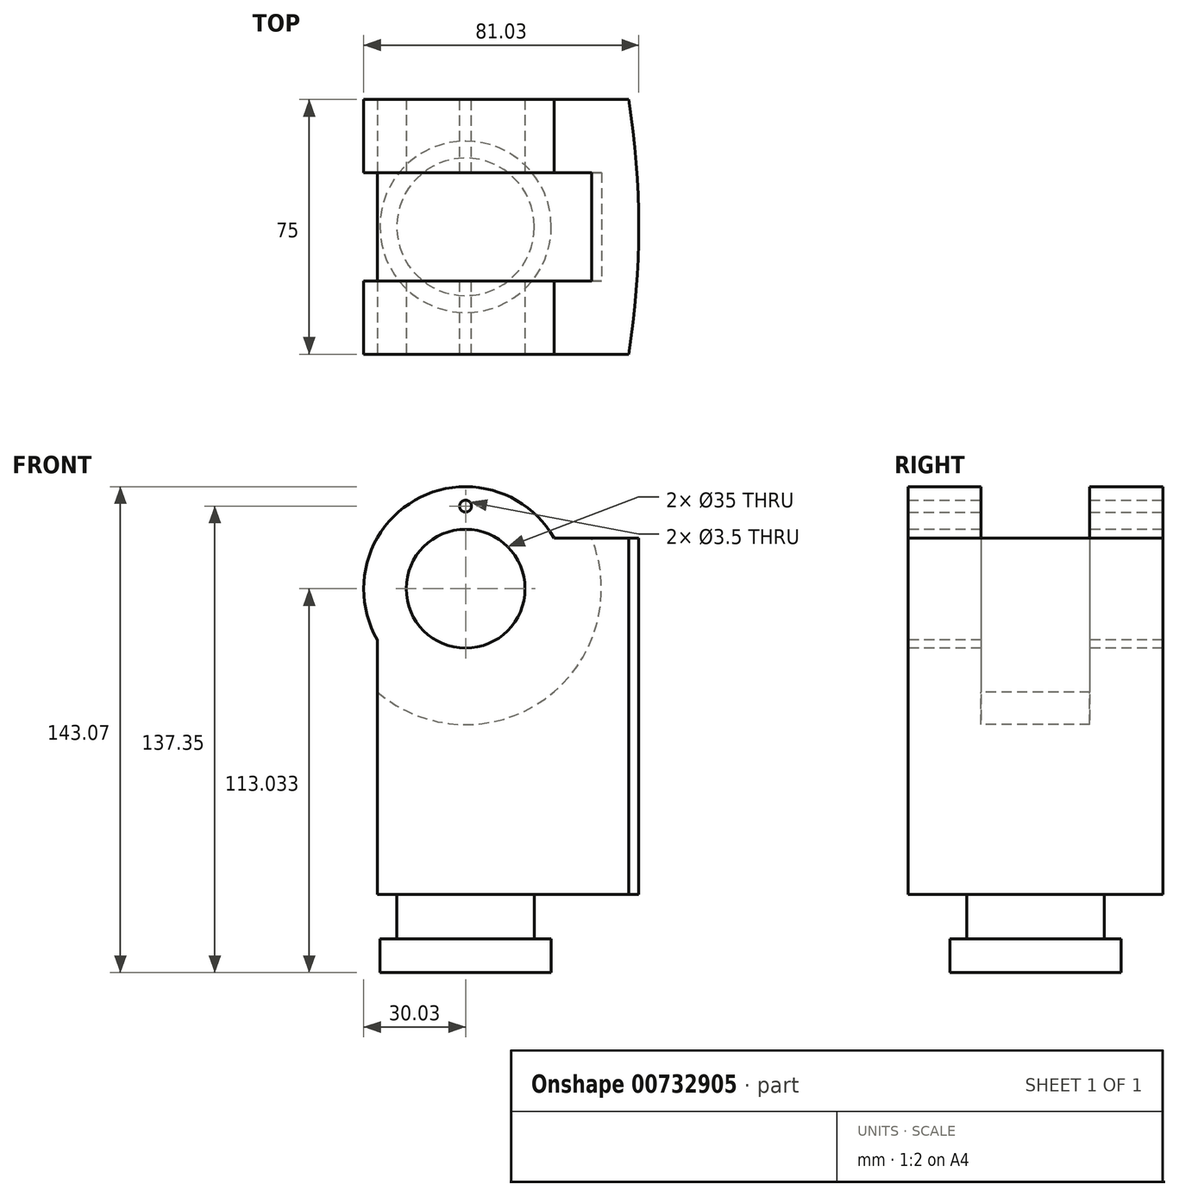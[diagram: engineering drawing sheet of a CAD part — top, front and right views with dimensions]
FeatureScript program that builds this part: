
annotation { "Feature Type Name" : "Feature", "Feature Type Description" : "" }
export const myFeature = defineFeature(function(context is Context, id is Id, definition is map)
    precondition{}
    {
        {
            var Q0;
            Q0=qCreatedBy(makeId("Top.planeOp"),FACE);
            var sketch = newSketch(context, id + "F0", { "sketchPlane" : qUnion([Q0])});
            skCircle(sketch, "E0", {"center": v(0, 0) * mm, "radius": 25.25 * mm});
            skSolve(sketch);
        }
        {
            var Q0;
            Q0 = qSketchRegion(id + "F0", true);
            extrude(context, id + "F1", {"entities" : qUnion([Q0]), "depth" : 10 * mm, "offsetDistance" : 25 * mm});
        }
        {
            var Q0;
            Q0=makeQuery(id+"F1.opExtrude","CAP_FACE",FACE,{"disambiguationData":[OSD([sQuery(id+"F0.wireOp",EDGE,"E0")])],"isStart":false});
            var sketch = newSketch(context, id + "F2", { "sketchPlane" : qUnion([Q0])});
            skCircle(sketch, "E1", {"center": v(0, 0) * mm, "radius": 20.25 * mm});
            skSolve(sketch);
        }
        {
            var Q0;
            Q0 = qSketchRegion(id + "F2", true);
            extrude(context, id + "F3", {"entities" : qUnion([Q0]), "operationType" : NewBodyOperationType.ADD, "depth" : 13 * mm, "offsetDistance" : 25 * mm});
        }
        {
            var Q0;
            Q0=makeQuery(id+"F3.opExtrude","CAP_FACE",FACE,{"disambiguationData":[OSD([sQuery(id+"F2.wireOp",EDGE,"E1")])],"isStart":false});
            var sketch = newSketch(context, id + "F4", { "sketchPlane" : qUnion([Q0])});
            skLineSegment(sketch, "E2.bottom", {"start": v(-26, 37.5) * mm, "end": v(26, 37.5) * mm});
            skLineSegment(sketch, "E2.top", {"start": v(-26, -37.5) * mm, "end": v(26, -37.5) * mm});
            skLineSegment(sketch, "E2.left", {"start": v(-26, 37.5) * mm, "end": v(-26, -37.5) * mm});
            skLineSegment(sketch, "E2.right", {"start": v(26, 37.5) * mm, "end": v(26, -37.5) * mm});
            skPoint(sketch, "E2.middle", {"position": v(0, 0) * mm});
            skSolve(sketch);
        }
        {
            var Q0;
            Q0=makeQuery(id+"F4.imprint","IMPRINT",FACE,{"disambiguationData":[TD([[makeQuery(id+"F4.imprint","IMPRINT",EDGE,{"derivedFrom":sQuery(id+"F4.wireOp",EDGE,"E2.bottom")}),-1.0]])]});
            var Q1;
            Q1=makeQuery(id+"F4.imprint","IMPRINT",FACE,{"disambiguationData":[TD([[makeQuery(id+"F4.imprint","IMPRINT",EDGE,{"derivedFrom":makeQuery(id+"F3.opExtrude","CAP_EDGE",EDGE,{"disambiguationData":[OSD([sQuery(id+"F2.wireOp",EDGE,"E1")])],"isStart":false})}),1.0]])]});
            extrude(context, id + "F5", {"entities" : qUnion([Q0, Q1]), "operationType" : NewBodyOperationType.ADD, "depth" : 60 * mm, "offsetDistance" : 25 * mm});
        }
        {
            var Q0;
            Q0=makeQuery(id+"F5.opExtrude","CAP_FACE",FACE,{"disambiguationData":[OSD([sQuery(id+"F4.wireOp",EDGE,"E2.bottom"),sQuery(id+"F4.wireOp",EDGE,"E2.top"),sQuery(id+"F4.wireOp",EDGE,"E2.left"),sQuery(id+"F4.wireOp",EDGE,"E2.right")])],"isStart":false});
            var sketch = newSketch(context, id + "F6", { "sketchPlane" : qUnion([Q0])});
            skLineSegment(sketch, "E3.bottom", {"start": v(-26, 16) * mm, "end": v(26, 16) * mm});
            skLineSegment(sketch, "E3.top", {"start": v(-26, -16) * mm, "end": v(26, -16) * mm});
            skLineSegment(sketch, "E3.left", {"start": v(-26, 16) * mm, "end": v(-26, -16) * mm});
            skLineSegment(sketch, "E3.right", {"start": v(26, 16) * mm, "end": v(26, -16) * mm});
            skPoint(sketch, "E3.middle", {"position": v(0, 0) * mm});
            skSolve(sketch);
        }
        {
            var Q0;
            {var subQ0=sQuery(id+"F6.wireOp",EDGE,"E3.bottom");Q0=makeQuery(id+"F6.imprint","IMPRINT",FACE,{"disambiguationData":[TD([[makeQuery(id+"F6.imprint","IMPRINT",EDGE,{"derivedFrom":subQ0}),1.0]])]});}
            var Q1;
            {var subQ0=sQuery(id+"F6.wireOp",EDGE,"E3.top");Q1=makeQuery(id+"F6.imprint","IMPRINT",FACE,{"disambiguationData":[TD([[makeQuery(id+"F6.imprint","IMPRINT",EDGE,{"derivedFrom":subQ0}),-1.0]])]});}
            extrude(context, id + "F7", {"entities" : qUnion([Q0, Q1]), "operationType" : NewBodyOperationType.ADD, "depth" : 15 * mm, "offsetDistance" : 25 * mm});
        }
        {
            var Q0;
            Q0=makeQuery(id+"F7.opExtrude","SWEPT_FACE",FACE,{"disambiguationData":[OSD([sQuery(id+"F6.wireOp",EDGE,"E3.bottom")])]});
            var sketch = newSketch(context, id + "F8", { "sketchPlane" : qUnion([Q0])});
            skCircle(sketch, "E4", {"center": v(0, 113.03) * mm, "radius": 30.03 * mm});
            skPoint(sketch, "E4.first.point", {"position": v(-26, 98) * mm});
            skPoint(sketch, "E4.second.point", {"position": v(0, 83) * mm});
            skPoint(sketch, "E4.third.point", {"position": v(26, 98) * mm});
            skSolve(sketch);
        }
        {
            var Q0;
            {var subQ1=sQuery(id+"F6.wireOp",EDGE,"E3.bottom");var subQ2=makeQuery(id+"F7.opExtrude","CAP_EDGE",EDGE,{"disambiguationData":[OSD([subQ1])],"isStart":false});Q0=makeQuery(id+"F8.imprint","IMPRINT",FACE,{"disambiguationData":[TD([[makeQuery(id+"F8.imprint","IMPRINT",EDGE,{"derivedFrom":subQ2}),1.0]])]});}
            extrude(context, id + "F9", {"entities" : qUnion([Q0]), "operationType" : NewBodyOperationType.ADD, "oppositeDirection" : true, "depth" : 21.5 * mm, "offsetDistance" : 25 * mm});
        }
        {
            var Q0;
            {var subQ0=sQuery(id+"F4.wireOp",EDGE,"E2.top");Q0=makeQuery(id+"F7.boolean.opBoolean","MERGE",FACE,{"derivedFrom":[makeQuery(id+"F5.opExtrude","SWEPT_FACE",FACE,{"disambiguationData":[OSD([subQ0])]}),makeQuery(id+"F7.opExtrude","SWEPT_FACE",FACE,{"disambiguationData":[OSD([subQ0])]})]});}
            var sketch = newSketch(context, id + "F10", { "sketchPlane" : qUnion([Q0])});
            skLineSegment(sketch, "E5", {"start": v(0, 98) * mm, "end": v(0, 83) * mm});
            skCircle(sketch, "E6", {"center": v(0, 113.03) * mm, "radius": 30.03 * mm});
            skPoint(sketch, "E6.first.point", {"position": v(-26, 98) * mm});
            skPoint(sketch, "E6.third.point", {"position": v(26, 98) * mm});
            skSolve(sketch);
        }
        {
            var Q0;
            Q0 = qSketchRegion(id + "F10", true);
            extrude(context, id + "F11", {"entities" : qUnion([Q0]), "operationType" : NewBodyOperationType.ADD, "oppositeDirection" : true, "depth" : 21.5 * mm, "offsetDistance" : 25 * mm});
        }
        {
            var Q0;
            {var subQ0=sQuery(id+"F4.wireOp",EDGE,"E2.top");Q0=makeQuery(id+"F11.boolean.opBoolean","MERGE",FACE,{"derivedFrom":[makeQuery(id+"F7.boolean.opBoolean","MERGE",FACE,{"derivedFrom":[makeQuery(id+"F5.opExtrude","SWEPT_FACE",FACE,{"disambiguationData":[OSD([subQ0])]}),makeQuery(id+"F7.opExtrude","SWEPT_FACE",FACE,{"disambiguationData":[OSD([subQ0])]})]}),makeQuery(id+"F11.opExtrude","CAP_FACE",FACE,{"disambiguationData":[OSD([sQuery(id+"F10.wireOp",EDGE,"E6")])],"isStart":true})]});}
            var sketch = newSketch(context, id + "F12", { "sketchPlane" : qUnion([Q0])});
            skCircle(sketch, "E7", {"center": v(0, 113.03) * mm, "radius": 17.5 * mm});
            skSolve(sketch);
        }
        {
            var Q0;
            Q0=makeQuery(id+"F12.imprint","IMPRINT",FACE,{"disambiguationData":[TD([[makeQuery(id+"F12.imprint","IMPRINT",EDGE,{"derivedFrom":sQuery(id+"F12.wireOp",EDGE,"E7")}),1.0]])]});
            extrude(context, id + "F13", {"entities" : qUnion([Q0]), "operationType" : NewBodyOperationType.REMOVE, "oppositeDirection" : true, "depth" : 84 * mm, "offsetDistance" : 25 * mm});
        }
        {
            var Q0;
            {var subQ0=sQuery(id+"F4.wireOp",EDGE,"E2.bottom");Q0=makeQuery(id+"F9.boolean.opBoolean","MERGE",FACE,{"derivedFrom":[makeQuery(id+"F7.boolean.opBoolean","MERGE",FACE,{"derivedFrom":[makeQuery(id+"F5.opExtrude","SWEPT_FACE",FACE,{"disambiguationData":[OSD([subQ0])]}),makeQuery(id+"F7.opExtrude","SWEPT_FACE",FACE,{"disambiguationData":[OSD([subQ0])]})]}),makeQuery(id+"F9.opExtrude","CAP_FACE",FACE,{"disambiguationData":[OSD([sQuery(id+"F6.wireOp",EDGE,"E3.bottom"),sQuery(id+"F8.wireOp",EDGE,"E4")])],"isStart":false})]});}
            var sketch = newSketch(context, id + "F14", { "sketchPlane" : qUnion([Q0])});
            skLineSegment(sketch, "E8", {"start": v(0, 137.35) * mm, "end": v(0, 130.53) * mm});
            skCircle(sketch, "E9", {"center": v(0, 137.35) * mm, "radius": 1.75 * mm});
            skSolve(sketch);
        }
        {
            var Q0;
            Q0 = qSketchRegion(id + "F14", true);
            extrude(context, id + "F15", {"entities" : qUnion([Q0]), "operationType" : NewBodyOperationType.REMOVE, "oppositeDirection" : true, "depth" : 80 * mm, "offsetDistance" : 25 * mm});
        }
        {
            var Q0;
            {var subQ0=sQuery(id+"F6.wireOp",EDGE,"E3.bottom");Q0=makeQuery(id+"F9.boolean.opBoolean","MERGE",FACE,{"derivedFrom":[makeQuery(id+"F7.opExtrude","SWEPT_FACE",FACE,{"disambiguationData":[OSD([subQ0])]}),makeQuery(id+"F9.opExtrude","CAP_FACE",FACE,{"disambiguationData":[OSD([subQ0,sQuery(id+"F8.wireOp",EDGE,"E4")])],"isStart":true})]});}
            var sketch = newSketch(context, id + "F16", { "sketchPlane" : qUnion([Q0])});
            skCircle(sketch, "E10", {"center": v(0, 113.03) * mm, "radius": 39.72 * mm});
            skSolve(sketch);
        }
        {
            var Q0;
            Q0 = qSketchRegion(id + "F16", true);
            extrude(context, id + "F17", {"entities" : qUnion([Q0]), "operationType" : NewBodyOperationType.REMOVE, "depth" : 32 * mm, "offsetDistance" : 25 * mm});
        }
        {
            var Q0;
            {var subQ0=sQuery(id+"F4.wireOp",EDGE,"E2.right");var subQ1=makeQuery(id+"F5.opExtrude","CAP_EDGE",EDGE,{"disambiguationData":[OSD([subQ0])],"isStart":false});Q0=makeQuery(id+"F7.boolean.opBoolean","MERGE",FACE,{"derivedFrom":[makeQuery(id+"F5.opExtrude","SWEPT_FACE",FACE,{"disambiguationData":[OSD([subQ0])]}),makeQuery(id+"F7.opExtrude","SWEPT_FACE",FACE,{"disambiguationData":[OSD([subQ0]),TDD([makeQuery(id+"F6.imprint","IMPRINT",EDGE,{"disambiguationData":[TD([[makeQuery(id+"F6.imprint","INTERSECT",VERTEX,{"derivedFrom":[makeQuery(id+"F5.opExtrude","CAP_EDGE",EDGE,{"disambiguationData":[OSD([sQuery(id+"F4.wireOp",EDGE,"E2.bottom")])],"isStart":false}),subQ1]}),-1.0]])],"derivedFrom":subQ1})])]}),makeQuery(id+"F7.opExtrude","SWEPT_FACE",FACE,{"disambiguationData":[OSD([subQ0]),TDD([makeQuery(id+"F6.imprint","IMPRINT",EDGE,{"disambiguationData":[TD([[makeQuery(id+"F6.imprint","INTERSECT",VERTEX,{"derivedFrom":[makeQuery(id+"F5.opExtrude","CAP_EDGE",EDGE,{"disambiguationData":[OSD([sQuery(id+"F4.wireOp",EDGE,"E2.top")])],"isStart":false}),subQ1]}),1.0]])],"derivedFrom":subQ1})])]})]});}
            var sketch = newSketch(context, id + "F18", { "sketchPlane" : qUnion([Q0])});
            skLineSegment(sketch, "E11.bottom", {"start": v(-37.5, 23) * mm, "end": v(37.5, 23) * mm});
            skLineSegment(sketch, "E11.top", {"start": v(-37.5, 83) * mm, "end": v(37.5, 83) * mm});
            skLineSegment(sketch, "E11.left", {"start": v(-37.5, 23) * mm, "end": v(-37.5, 83) * mm});
            skLineSegment(sketch, "E11.right", {"start": v(37.5, 23) * mm, "end": v(37.5, 83) * mm});
            skSolve(sketch);
        }
        {
            var Q0;
            Q0 = qSketchRegion(id + "F18", true);
            extrude(context, id + "F19", {"entities" : qUnion([Q0]), "operationType" : NewBodyOperationType.ADD, "depth" : 22 * mm, "offsetDistance" : 25 * mm});
        }
        {
            var Q0;
            Q0=makeQuery(id+"F19.boolean.opBoolean","MERGE",FACE,{"derivedFrom":[makeQuery(id+"F5.opExtrude","CAP_FACE",FACE,{"disambiguationData":[OSD([sQuery(id+"F4.wireOp",EDGE,"E2.bottom"),sQuery(id+"F4.wireOp",EDGE,"E2.top"),sQuery(id+"F4.wireOp",EDGE,"E2.left"),sQuery(id+"F4.wireOp",EDGE,"E2.right")])],"isStart":true}),makeQuery(id+"F19.opExtrude","SWEPT_FACE",FACE,{"disambiguationData":[OSD([sQuery(id+"F18.wireOp",EDGE,"E11.bottom")])]})]});
            var sketch = newSketch(context, id + "F20", { "sketchPlane" : qUnion([Q0])});
            skLineSegment(sketch, "E12", {"start": v(48, 0) * mm, "end": v(51, 0) * mm});
            skCircle(sketch, "E13", {"center": v(-184.88, 0) * mm, "radius": 235.88 * mm});
            skPoint(sketch, "E13.first.point", {"position": v(48, 37.5) * mm});
            skPoint(sketch, "E13.third.point", {"position": v(48, -37.5) * mm});
            skSolve(sketch);
        }
        {
            var Q0;
            {var subQ0=sQuery(id+"F20.wireOp",EDGE,"E12");Q0=makeQuery(id+"F20.imprint","IMPRINT",FACE,{"disambiguationData":[TD([[makeQuery(id+"F20.imprint","IMPRINT",EDGE,{"derivedFrom":subQ0}),1.0]])]});}
            var Q1;
            {var subQ0=sQuery(id+"F20.wireOp",EDGE,"E12");Q1=makeQuery(id+"F20.imprint","IMPRINT",FACE,{"disambiguationData":[TD([[makeQuery(id+"F20.imprint","IMPRINT",EDGE,{"derivedFrom":subQ0}),-1.0]])]});}
            extrude(context, id + "F21", {"entities" : qUnion([Q0, Q1]), "operationType" : NewBodyOperationType.ADD, "oppositeDirection" : true, "depth" : 60 * mm, "offsetDistance" : 25 * mm});
        }
        {
            var Q0;
            Q0=makeQuery(id+"F21.boolean.opBoolean","MERGE",FACE,{"derivedFrom":[makeQuery(id+"F19.opExtrude","SWEPT_FACE",FACE,{"disambiguationData":[OSD([sQuery(id+"F18.wireOp",EDGE,"E11.top")])]}),makeQuery(id+"F21.opExtrude","CAP_FACE",FACE,{"disambiguationData":[OSD([sQuery(id+"F18.wireOp",EDGE,"E11.bottom"),sQuery(id+"F20.wireOp",EDGE,"E13"),dummyQuery(id+"F20.imprint",EDGE)])],"isStart":false})]});
            var sketch = newSketch(context, id + "F22", { "sketchPlane" : qUnion([Q0])});
            skLineSegment(sketch, "E14", {"start": v(48, 37.5) * mm, "end": v(26, 37.5) * mm});
            skLineSegment(sketch, "E15", {"start": v(26, 37.5) * mm, "end": v(26, -37.5) * mm});
            skLineSegment(sketch, "E16", {"start": v(26, 16) * mm, "end": v(26, 16) * mm});
            skLineSegment(sketch, "E17", {"start": v(26, -16) * mm, "end": v(26, -16) * mm});
            skSolve(sketch);
        }
        {
            var Q0;
            Q0 = qSketchRegion(id + "F22", true);
            var Q1;
            Q1=makeQuery(id+"F22.imprint","IMPRINT",FACE,{"disambiguationData":[TD([[makeQuery(id+"F22.imprint","IMPRINT",EDGE,{"derivedFrom":sQuery(id+"F22.wireOp",EDGE,"E14")}),1.0]])]});
            var Q2;
            {var subQ7=sQuery(id+"F22.wireOp",EDGE,"E16");Q2=makeQuery(id+"F22.imprint","IMPRINT",FACE,{"disambiguationData":[TD([[makeQuery(id+"F22.imprint","IMPRINT",EDGE,{"derivedFrom":subQ7}),1.0]])]});}
            var Q3;
            {var subQ7=sQuery(id+"F22.wireOp",EDGE,"E17");Q3=makeQuery(id+"F22.imprint","IMPRINT",FACE,{"disambiguationData":[TD([[makeQuery(id+"F22.imprint","IMPRINT",EDGE,{"derivedFrom":subQ7}),-1.0]])]});}
            extrude(context, id + "F23", {"entities" : qUnion([Q0, Q1, Q2, Q3]), "operationType" : NewBodyOperationType.ADD, "depth" : 45 * mm, "offsetDistance" : 25 * mm});
        }
        {
            var Q0;
            Q0=qCreatedBy(makeId("Top.planeOp"),FACE);
            cPlane(context, id + "F24", {"entities" : qUnion([Q0]), "cplaneType" : CPlaneType.OFFSET, "offset" : 66.6 * mm, "width" : 150 * mm, "height" : 150 * mm});
        }
        {
            var Q0;
            Q0=makeQuery(id+"F17.boolean.opBoolean","MERGE",FACE,{"derivedFrom":[makeQuery(id+"F11.boolean.opBoolean","MERGE",FACE,{"derivedFrom":[makeQuery(id+"F7.opExtrude","SWEPT_FACE",FACE,{"disambiguationData":[OSD([sQuery(id+"F6.wireOp",EDGE,"E3.top")])]}),makeQuery(id+"F11.opExtrude","CAP_FACE",FACE,{"disambiguationData":[OSD([sQuery(id+"F10.wireOp",EDGE,"E6")])],"isStart":false})]})],"fromTools":[makeQuery(id+"F17.opExtrude","CAP_FACE",FACE,{"disambiguationData":[OSD([sQuery(id+"F16.wireOp",EDGE,"E10")])],"isStart":false})]});
            var sketch = newSketch(context, id + "F25", { "sketchPlane" : qUnion([Q0])});
            skCircle(sketch, "E18", {"center": v(0, 113.03) * mm, "radius": 40 * mm});
            skSolve(sketch);
        }
        {
            var Q0;
            Q0 = qSketchRegion(id + "F25", true);
            extrude(context, id + "F26", {"entities" : qUnion([Q0]), "operationType" : NewBodyOperationType.REMOVE, "depth" : 32 * mm, "offsetDistance" : 25 * mm});
        }
    });
